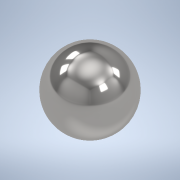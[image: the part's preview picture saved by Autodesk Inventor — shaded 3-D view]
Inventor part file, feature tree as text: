
AUTODESK INVENTOR PART (.ipt)
format: ipt  version: 2020 (Build 240168000, 168)  size: 122,880 bytes
history: native  units: mm
features: revolve x1, sketch x1
ambient origin geometry x8: Origin, YZ Plane, XZ Plane, XY Plane, X Axis, Y Axis, Z Axis, Center Point
bodies: Solid1 (feature_tree)
feature tree (2):
  revolve  "Revolution1"  Angle=90.0deg
  sketch  "Sketch1"  dims[d0=10.0mm d1=90.0deg]
